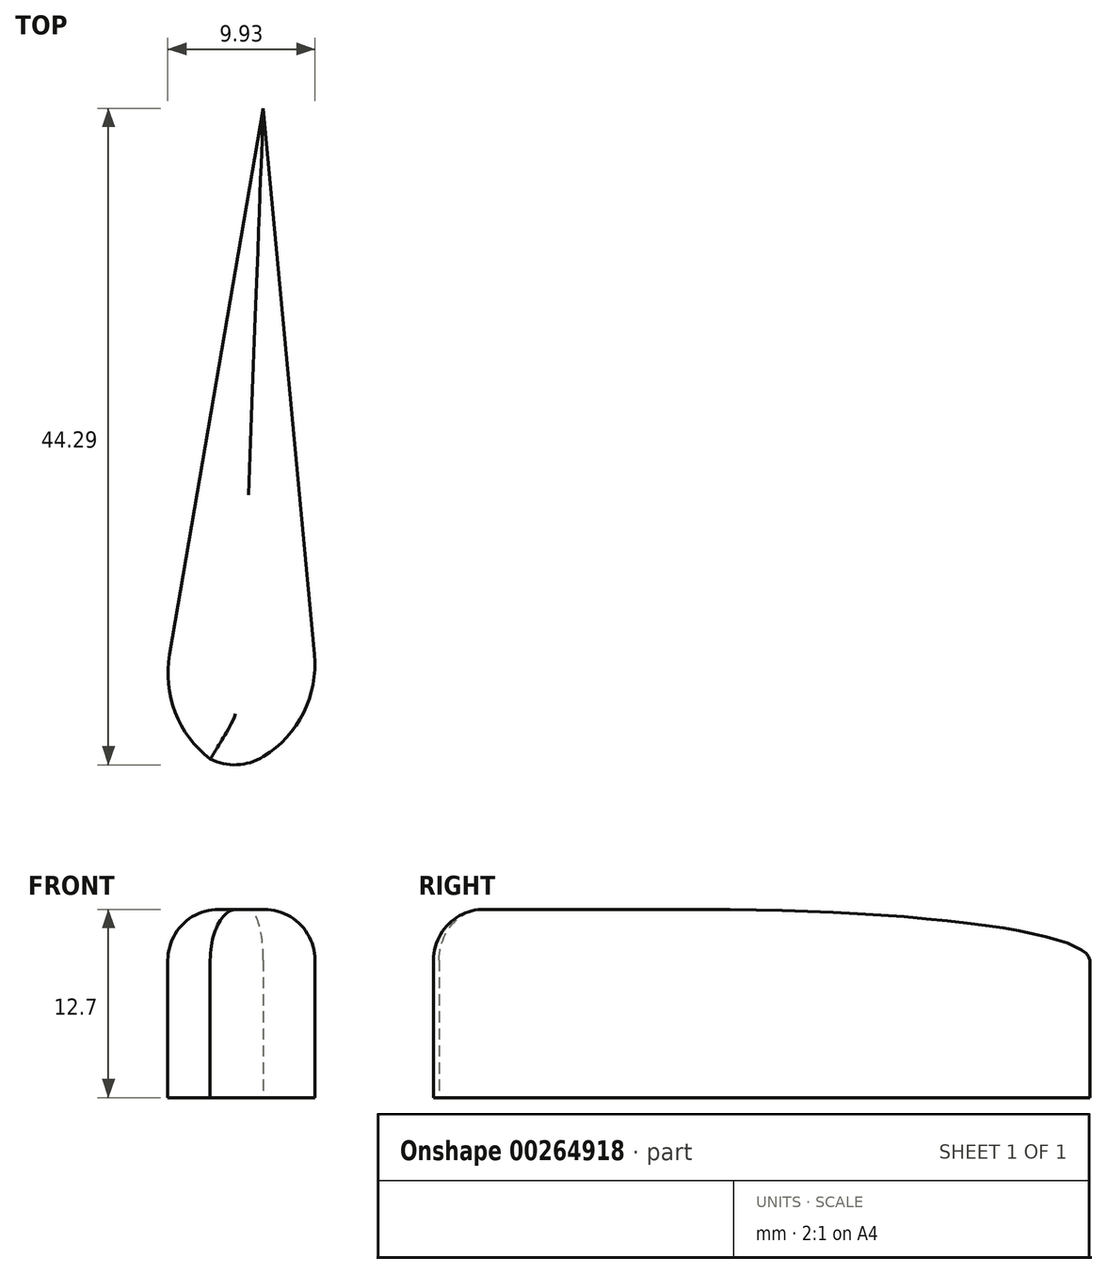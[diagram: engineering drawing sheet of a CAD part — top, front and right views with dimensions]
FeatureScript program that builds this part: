
annotation { "Feature Type Name" : "Feature", "Feature Type Description" : "" }
export const myFeature = defineFeature(function(context is Context, id is Id, definition is map)
    precondition{}
    {
        {
            var Q0;
            Q0=qCreatedBy(makeId("Top.planeOp"),FACE);
            var sketch = newSketch(context, id + "F0", { "sketchPlane" : qUnion([Q0])});
            skLineSegment(sketch, "E0", {"start": v(-19.57, 0) * mm, "end": v(-13.24, 36.84) * mm});
            skLineSegment(sketch, "E1", {"start": v(-13.24, 36.84) * mm, "end": v(-9.79, 0) * mm});
            skArc(sketch, "E2", {"start": v(-19.57, 0) * mm, "mid": v(-19.18, -3.91) * mm, "end": v(-16.82, -7.06) * mm});
            skArc(sketch, "E3", {"start": v(-13.24, -6.9) * mm, "mid": v(-10.52, -3.95) * mm, "end": v(-9.79, 0) * mm});
            skArc(sketch, "E4", {"start": v(-16.82, -7.06) * mm, "mid": v(-15.01, -7.45) * mm, "end": v(-13.24, -6.9) * mm});
            skSolve(sketch);
        }
        {
            var Q0;
            Q0=makeQuery(id+"F0.imprint","IMPRINT",FACE,{"disambiguationData":[TD([[makeQuery(id+"F0.imprint","IMPRINT",EDGE,{"derivedFrom":sQuery(id+"F0.wireOp",EDGE,"E0")}),-1.0]])]});
            extrude(context, id + "F1", {"entities" : qUnion([Q0]), "depth" : 12.7 * mm});
        }
        {
            var Q0;
            Q0=makeQuery(id+"F1.opExtrude","CAP_EDGE",EDGE,{"disambiguationData":[OSD([sQuery(id+"F0.wireOp",EDGE,"E0")])],"isStart":false});
            var Q1;
            Q1=makeQuery(id+"F1.opExtrude","CAP_EDGE",EDGE,{"disambiguationData":[OSD([sQuery(id+"F0.wireOp",EDGE,"E1")])],"isStart":false});
            var Q2;
            Q2=makeQuery(id+"F1.opExtrude","CAP_EDGE",EDGE,{"disambiguationData":[OSD([sQuery(id+"F0.wireOp",EDGE,"E3")])],"isStart":false});
            var Q3;
            Q3=makeQuery(id+"F1.opExtrude","CAP_EDGE",EDGE,{"disambiguationData":[OSD([sQuery(id+"F0.wireOp",EDGE,"E2")])],"isStart":false});
            fillet(context, id + "F2", {"entities" : qUnion([Q0, Q1, Q2, Q3]), "radius" : 3.43 * mm, "tangentPropagation" : true, "allowEdgeOverflow" : false});
        }
    });
